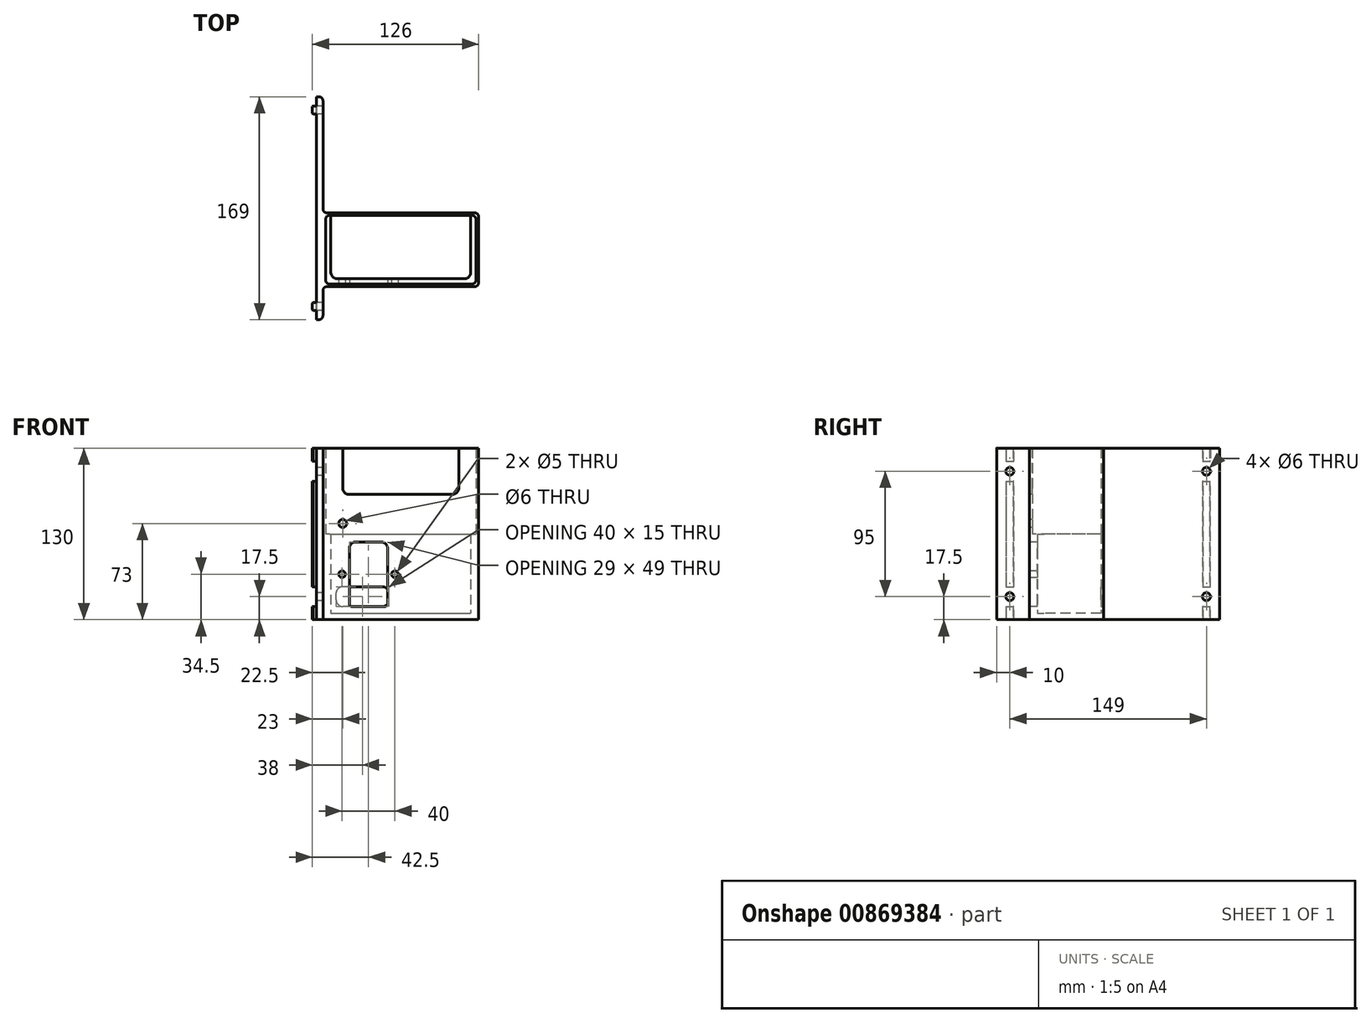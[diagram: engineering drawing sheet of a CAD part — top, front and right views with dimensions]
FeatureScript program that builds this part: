
annotation { "Feature Type Name" : "Feature", "Feature Type Description" : "" }
export const myFeature = defineFeature(function(context is Context, id is Id, definition is map)
    precondition{}
    {
        {
            var Q0;
            Q0=qCreatedBy(makeId("Top.planeOp"),FACE);
            var sketch = newSketch(context, id + "F0", { "sketchPlane" : qUnion([Q0])});
            skLineSegment(sketch, "E0.bottom", {"start": v(-57, 25) * mm, "end": v(57, 25) * mm});
            skLineSegment(sketch, "E0.top", {"start": v(-57, -27) * mm, "end": v(57, -27) * mm});
            skLineSegment(sketch, "E0.left", {"start": v(-57, 25) * mm, "end": v(-57, -27) * mm});
            skLineSegment(sketch, "E0.right", {"start": v(57, 25) * mm, "end": v(57, -27) * mm});
            skLineSegment(sketch, "E1.0", {"start": v(-59, 27) * mm, "end": v(59, 27) * mm});
            skLineSegment(sketch, "E1.1", {"start": v(-59, 27) * mm, "end": v(-59, -29) * mm});
            skLineSegment(sketch, "E1.2", {"start": v(-59, -29) * mm, "end": v(59, -29) * mm});
            skLineSegment(sketch, "E1.3", {"start": v(59, 27) * mm, "end": v(59, -29) * mm});
            skLineSegment(sketch, "E2.bottom", {"start": v(-57, 25) * mm, "end": v(-53, 25) * mm});
            skLineSegment(sketch, "E2.top", {"start": v(-57, -27) * mm, "end": v(-53, -27) * mm});
            skLineSegment(sketch, "E2.right", {"start": v(-53, 25) * mm, "end": v(-53, -23) * mm});
            skLineSegment(sketch, "E3.MirrorCS", {"start": v(53, 25) * mm, "end": v(53, -23) * mm});
            skLineSegment(sketch, "E4", {"start": v(-59, -54) * mm, "end": v(-59, 115) * mm});
            skLineSegment(sketch, "E5", {"start": v(-59, 115) * mm, "end": v(-64, 115) * mm});
            skLineSegment(sketch, "E6", {"start": v(-64, 115) * mm, "end": v(-64, -54) * mm});
            skLineSegment(sketch, "E7", {"start": v(-64, -54) * mm, "end": v(-59, -54) * mm});
            skLineSegment(sketch, "E8.bottom", {"start": v(-64, -47) * mm, "end": v(-67, -47) * mm});
            skLineSegment(sketch, "E8.top", {"start": v(-64, -41) * mm, "end": v(-67, -41) * mm});
            skLineSegment(sketch, "E8.left", {"start": v(-64, -47) * mm, "end": v(-64, -41) * mm});
            skLineSegment(sketch, "E8.right", {"start": v(-67, -47) * mm, "end": v(-67, -41) * mm});
            skLineSegment(sketch, "E9.bottom", {"start": v(-64, 108) * mm, "end": v(-67, 108) * mm});
            skLineSegment(sketch, "E9.top", {"start": v(-64, 102) * mm, "end": v(-67, 102) * mm});
            skLineSegment(sketch, "E9.left", {"start": v(-64, 108) * mm, "end": v(-64, 102) * mm});
            skLineSegment(sketch, "E9.right", {"start": v(-67, 108) * mm, "end": v(-67, 102) * mm});
            skLineSegment(sketch, "E10", {"start": v(-53, -23) * mm, "end": v(53, -23) * mm});
            skPoint(sketch, "E11.orphan", {"position": v(53, -27) * mm});
            skSolve(sketch);
        }
        {
            var Q0;
            {var subQ2=sQuery(id+"F0.wireOp",EDGE,"E1.1");Q0=makeQuery(id+"F0.imprint","IMPRINT",FACE,{"disambiguationData":[TD([[makeQuery(id+"F0.imprint","IMPRINT",EDGE,{"derivedFrom":subQ2}),-1.0]])]});}
            var Q1;
            {var subQ0=sQuery(id+"F0.wireOp",EDGE,"E8.bottom");Q1=makeQuery(id+"F0.imprint","IMPRINT",FACE,{"disambiguationData":[TD([[makeQuery(id+"F0.imprint","IMPRINT",EDGE,{"derivedFrom":subQ0}),-1.0]])]});}
            var Q2;
            {var subQ2=sQuery(id+"F0.wireOp",EDGE,"E9.bottom");Q2=makeQuery(id+"F0.imprint","IMPRINT",FACE,{"disambiguationData":[TD([[makeQuery(id+"F0.imprint","IMPRINT",EDGE,{"derivedFrom":subQ2}),1.0]])]});}
            var Q3;
            {var subQ1=sQuery(id+"F0.wireOp",EDGE,"E0.left");Q3=makeQuery(id+"F0.imprint","IMPRINT",FACE,{"disambiguationData":[TD([[makeQuery(id+"F0.imprint","IMPRINT",EDGE,{"derivedFrom":subQ1}),-1.0]])]});}
            extrude(context, id + "F1", {"entities" : qUnion([Q0, Q1, Q2, Q3]), "depth" : 130 * mm, "offsetDistance" : 25 * mm});
        }
        {
            var Q0;
            {var subQ2=sQuery(id+"F0.wireOp",EDGE,"E0.left");Q0=makeQuery(id+"F0.imprint","IMPRINT",FACE,{"disambiguationData":[TD([[makeQuery(id+"F0.imprint","IMPRINT",EDGE,{"derivedFrom":subQ2}),1.0]])]});}
            var Q1;
            {var subQ2=sQuery(id+"F0.wireOp",EDGE,"E0.left");Q1=makeQuery(id+"F0.imprint","IMPRINT",FACE,{"disambiguationData":[TD([[makeQuery(id+"F0.imprint","IMPRINT",EDGE,{"derivedFrom":subQ2}),1.0]])]});}
            extrude(context, id + "F2", {"entities" : qUnion([Q0, Q1]), "operationType" : NewBodyOperationType.ADD, "depth" : 65 * mm, "offsetDistance" : 25 * mm});
        }
        {
            var Q0;
            {var subQ0=sQuery(id+"F0.wireOp",EDGE,"E2.right");Q0=makeQuery(id+"F0.imprint","IMPRINT",FACE,{"disambiguationData":[TD([[makeQuery(id+"F0.imprint","IMPRINT",EDGE,{"derivedFrom":subQ0}),1.0]])]});}
            extrude(context, id + "F3", {"entities" : qUnion([Q0]), "operationType" : NewBodyOperationType.ADD, "depth" : 5 * mm, "offsetDistance" : 25 * mm});
        }
        {
            var Q0;
            Q0=makeQuery(id+"F1.opExtrude","SWEPT_FACE",FACE,{"disambiguationData":[OSD([sQuery(id+"F0.wireOp",EDGE,"E1.2")])]});
            var sketch = newSketch(context, id + "F4", { "sketchPlane" : qUnion([Q0])});
            skLineSegment(sketch, "E12.bottom", {"start": v(-34, 59) * mm, "end": v(-15, 59) * mm});
            skLineSegment(sketch, "E12.top", {"start": v(-37, 10) * mm, "end": v(-12, 10) * mm});
            skLineSegment(sketch, "E12.left", {"start": v(-39, 54) * mm, "end": v(-39, 12) * mm});
            skLineSegment(sketch, "E12.right", {"start": v(-10, 54) * mm, "end": v(-10, 12) * mm});
            skCircle(sketch, "E13", {"center": v(-44.5, 34.5) * mm, "radius": 2.5 * mm});
            skPoint(sketch, "E13.centerSnap0", {"position": v(-39, 34.5) * mm});
            skCircle(sketch, "E14", {"center": v(-4.5, 34.5) * mm, "radius": 2.5 * mm});
            skPoint(sketch, "E14.centerSnap0", {"position": v(-10, 34.5) * mm});
            skPoint(sketch, "E15.visualSharp", {"position": v(-10, 59) * mm});
            skArc(sketch, "E15.filletArc", {"start": v(-10, 54) * mm, "mid": v(-11.46, 57.54) * mm, "end": v(-15, 59) * mm});
            skPoint(sketch, "E16.visualSharp", {"position": v(-39, 59) * mm});
            skArc(sketch, "E16.filletArc", {"start": v(-34, 59) * mm, "mid": v(-37.54, 57.54) * mm, "end": v(-39, 54) * mm});
            skPoint(sketch, "E17.visualSharp", {"position": v(-39, 10) * mm});
            skArc(sketch, "E17.filletArc", {"start": v(-39, 12) * mm, "mid": v(-38.41, 10.59) * mm, "end": v(-37, 10) * mm});
            skPoint(sketch, "E18.visualSharp", {"position": v(-10, 10) * mm});
            skArc(sketch, "E18.filletArc", {"start": v(-12, 10) * mm, "mid": v(-10.59, 10.59) * mm, "end": v(-10, 12) * mm});
            skLineSegment(sketch, "E19.bottom", {"start": v(-44, 130) * mm, "end": v(44, 130) * mm});
            skLineSegment(sketch, "E19.top", {"start": v(-44, 95) * mm, "end": v(44, 95) * mm});
            skLineSegment(sketch, "E19.left", {"start": v(-44, 130) * mm, "end": v(-44, 95) * mm});
            skLineSegment(sketch, "E19.right", {"start": v(44, 130) * mm, "end": v(44, 95) * mm});
            skCircle(sketch, "E20", {"center": v(-44, 73) * mm, "radius": 3 * mm});
            skSolve(sketch);
        }
        {
            var Q0;
            Q0=makeQuery(id+"F4.imprint","IMPRINT",FACE,{"disambiguationData":[TD([[makeQuery(id+"F4.imprint","IMPRINT",EDGE,{"derivedFrom":sQuery(id+"F4.wireOp",EDGE,"E12.bottom")}),-1.0]])]});
            var Q1;
            Q1=makeQuery(id+"F4.imprint","IMPRINT",FACE,{"disambiguationData":[TD([[makeQuery(id+"F4.imprint","IMPRINT",EDGE,{"derivedFrom":sQuery(id+"F4.wireOp",EDGE,"E13")}),1.0]])]});
            var Q2;
            Q2=makeQuery(id+"F4.imprint","IMPRINT",FACE,{"disambiguationData":[TD([[makeQuery(id+"F4.imprint","IMPRINT",EDGE,{"derivedFrom":sQuery(id+"F4.wireOp",EDGE,"E14")}),1.0]])]});
            var Q3;
            Q3=makeQuery(id+"F4.imprint","IMPRINT",FACE,{"disambiguationData":[TD([[makeQuery(id+"F4.imprint","IMPRINT",EDGE,{"derivedFrom":sQuery(id+"F4.wireOp",EDGE,"E19.bottom")}),-1.0]])]});
            var Q4;
            Q4=makeQuery(id+"F4.imprint","IMPRINT",FACE,{"disambiguationData":[TD([[makeQuery(id+"F4.imprint","IMPRINT",EDGE,{"derivedFrom":sQuery(id+"F4.wireOp",EDGE,"E20")}),1.0]])]});
            extrude(context, id + "F5", {"entities" : qUnion([Q0, Q1, Q2, Q3, Q4]), "operationType" : NewBodyOperationType.REMOVE, "oppositeDirection" : true, "depth" : 10 * mm, "offsetDistance" : 25 * mm});
        }
        {
            var Q0;
            Q0=makeQuery(id+"F1.opExtrude","SWEPT_FACE",FACE,{"disambiguationData":[OSD([sQuery(id+"F0.wireOp",EDGE,"E1.0")])]});
            var sketch = newSketch(context, id + "F6", { "sketchPlane" : qUnion([Q0])});
            skLineSegment(sketch, "E21.bottom", {"start": v(9, 10) * mm, "end": v(49, 10) * mm});
            skLineSegment(sketch, "E21.top", {"start": v(9, 25) * mm, "end": v(49, 25) * mm});
            skLineSegment(sketch, "E21.left", {"start": v(9, 10) * mm, "end": v(9, 25) * mm});
            skLineSegment(sketch, "E21.right", {"start": v(49, 10) * mm, "end": v(49, 25) * mm});
            skSolve(sketch);
        }
        {
            var Q0;
            Q0=makeQuery(id+"F6.imprint","IMPRINT",FACE,{"disambiguationData":[TD([[makeQuery(id+"F6.imprint","IMPRINT",EDGE,{"derivedFrom":sQuery(id+"F6.wireOp",EDGE,"E21.bottom")}),1.0]])]});
            extrude(context, id + "F7", {"entities" : qUnion([Q0]), "operationType" : NewBodyOperationType.REMOVE, "oppositeDirection" : true, "depth" : 5 * mm, "offsetDistance" : 25 * mm});
        }
        {
            var Q0;
            Q0=makeQuery(id+"F1.opExtrude","SWEPT_FACE",FACE,{"disambiguationData":[OSD([sQuery(id+"F0.wireOp",EDGE,"E9.bottom")])]});
            var sketch = newSketch(context, id + "F8", { "sketchPlane" : qUnion([Q0])});
            skLineSegment(sketch, "E22.bottom", {"start": v(64, 120) * mm, "end": v(74, 120) * mm});
            skLineSegment(sketch, "E22.top", {"start": v(64, 105) * mm, "end": v(74, 105) * mm});
            skLineSegment(sketch, "E22.left", {"start": v(64, 120) * mm, "end": v(64, 105) * mm});
            skLineSegment(sketch, "E22.right", {"start": v(74, 120) * mm, "end": v(74, 105) * mm});
            skLineSegment(sketch, "E23.bottom", {"start": v(64, 10) * mm, "end": v(74, 10) * mm});
            skLineSegment(sketch, "E23.top", {"start": v(64, 25) * mm, "end": v(74, 25) * mm});
            skLineSegment(sketch, "E23.left", {"start": v(64, 10) * mm, "end": v(64, 25) * mm});
            skLineSegment(sketch, "E23.right", {"start": v(74, 10) * mm, "end": v(74, 25) * mm});
            skSolve(sketch);
        }
        {
            var Q0;
            {var subQ0=sQuery(id+"F8.wireOp",EDGE,"E23.left");Q0=makeQuery(id+"F8.imprint","IMPRINT",FACE,{"disambiguationData":[TD([[makeQuery(id+"F8.imprint","IMPRINT",EDGE,{"derivedFrom":subQ0}),1.0]])]});}
            var Q1;
            {var subQ0=sQuery(id+"F8.wireOp",EDGE,"E22.left");Q1=makeQuery(id+"F8.imprint","IMPRINT",FACE,{"disambiguationData":[TD([[makeQuery(id+"F8.imprint","IMPRINT",EDGE,{"derivedFrom":subQ0}),1.0]])]});}
            extrude(context, id + "F9", {"entities" : qUnion([Q0, Q1]), "operationType" : NewBodyOperationType.REMOVE, "oppositeDirection" : true, "depth" : 200 * mm, "offsetDistance" : 25 * mm});
        }
        {
            var Q0;
            Q0=makeQuery(id+"F1.opExtrude","SWEPT_EDGE",EDGE,{"disambiguationData":[OSD([sQuery(id+"F0.wireOp",EDGE,"E1.1"),sQuery(id+"F0.wireOp",EDGE,"E1.2"),sQuery(id+"F0.wireOp",EDGE,"E4")])]});
            var Q1;
            Q1=makeQuery(id+"F1.opExtrude","SWEPT_EDGE",EDGE,{"disambiguationData":[OSD([sQuery(id+"F0.wireOp",EDGE,"E1.0"),sQuery(id+"F0.wireOp",EDGE,"E1.1"),sQuery(id+"F0.wireOp",EDGE,"E4")])]});
            var Q2;
            Q2=makeQuery(id+"F1.opExtrude","SWEPT_EDGE",EDGE,{"disambiguationData":[OSD([sQuery(id+"F0.wireOp",EDGE,"E1.0"),sQuery(id+"F0.wireOp",EDGE,"E1.3")])]});
            var Q3;
            Q3=makeQuery(id+"F1.opExtrude","SWEPT_EDGE",EDGE,{"disambiguationData":[OSD([sQuery(id+"F0.wireOp",EDGE,"E1.2"),sQuery(id+"F0.wireOp",EDGE,"E1.3")])]});
            var Q4;
            Q4=makeQuery(id+"F1.opExtrude","SWEPT_EDGE",EDGE,{"disambiguationData":[OSD([sQuery(id+"F0.wireOp",EDGE,"E0.top"),sQuery(id+"F0.wireOp",EDGE,"E0.right")])]});
            var Q5;
            Q5=makeQuery(id+"F1.opExtrude","SWEPT_EDGE",EDGE,{"disambiguationData":[OSD([sQuery(id+"F0.wireOp",EDGE,"E0.bottom"),sQuery(id+"F0.wireOp",EDGE,"E0.right")])]});
            var Q6;
            Q6=makeQuery(id+"F1.opExtrude","SWEPT_EDGE",EDGE,{"disambiguationData":[OSD([sQuery(id+"F0.wireOp",EDGE,"E0.top"),sQuery(id+"F0.wireOp",EDGE,"E0.left")])]});
            var Q7;
            Q7=makeQuery(id+"F1.opExtrude","SWEPT_EDGE",EDGE,{"disambiguationData":[OSD([sQuery(id+"F0.wireOp",EDGE,"E0.bottom"),sQuery(id+"F0.wireOp",EDGE,"E0.left")])]});
            var Q8;
            Q8=makeQuery(id+"F1.opExtrude","SWEPT_EDGE",EDGE,{"disambiguationData":[OSD([sQuery(id+"F0.wireOp",EDGE,"E4"),sQuery(id+"F0.wireOp",EDGE,"E7")])]});
            var Q9;
            Q9=makeQuery(id+"F1.opExtrude","SWEPT_EDGE",EDGE,{"disambiguationData":[OSD([sQuery(id+"F0.wireOp",EDGE,"E4"),sQuery(id+"F0.wireOp",EDGE,"E5")])]});
            fillet(context, id + "F10", {"entities" : qUnion([Q0, Q1, Q2, Q3, Q4, Q5, Q6, Q7, Q8, Q9]), "radius" : 3 * mm, "tangentPropagation" : true, "allowEdgeOverflow" : false});
        }
        {
            var Q0;
            Q0=makeQuery(id+"F7.boolean.opBoolean","COPY",EDGE,{"derivedFrom":makeQuery(id+"F7.opExtrude","SWEPT_EDGE",EDGE,{"disambiguationData":[OSD([sQuery(id+"F6.wireOp",EDGE,"E21.top"),sQuery(id+"F6.wireOp",EDGE,"E21.left")])]})});
            var Q1;
            Q1=makeQuery(id+"F7.boolean.opBoolean","COPY",EDGE,{"derivedFrom":makeQuery(id+"F7.opExtrude","SWEPT_EDGE",EDGE,{"disambiguationData":[OSD([sQuery(id+"F6.wireOp",EDGE,"E21.bottom"),sQuery(id+"F6.wireOp",EDGE,"E21.left")])]})});
            var Q2;
            Q2=makeQuery(id+"F7.boolean.opBoolean","COPY",EDGE,{"derivedFrom":makeQuery(id+"F7.opExtrude","SWEPT_EDGE",EDGE,{"disambiguationData":[OSD([sQuery(id+"F6.wireOp",EDGE,"E21.bottom"),sQuery(id+"F6.wireOp",EDGE,"E21.right")])]})});
            var Q3;
            Q3=makeQuery(id+"F7.boolean.opBoolean","COPY",EDGE,{"derivedFrom":makeQuery(id+"F7.opExtrude","SWEPT_EDGE",EDGE,{"disambiguationData":[OSD([sQuery(id+"F6.wireOp",EDGE,"E21.top"),sQuery(id+"F6.wireOp",EDGE,"E21.right")])]})});
            var Q4;
            Q4=makeQuery(id+"F5.boolean.opBoolean","COPY",EDGE,{"derivedFrom":makeQuery(id+"F5.opExtrude","SWEPT_EDGE",EDGE,{"disambiguationData":[OSD([sQuery(id+"F4.wireOp",EDGE,"E19.top"),sQuery(id+"F4.wireOp",EDGE,"E19.left")])]})});
            var Q5;
            Q5=makeQuery(id+"F5.boolean.opBoolean","COPY",EDGE,{"derivedFrom":makeQuery(id+"F5.opExtrude","SWEPT_EDGE",EDGE,{"disambiguationData":[OSD([sQuery(id+"F4.wireOp",EDGE,"E19.top"),sQuery(id+"F4.wireOp",EDGE,"E19.right")])]})});
            var Q6;
            Q6=makeQuery(id+"F5.boolean.opBoolean","COPY",EDGE,{"derivedFrom":makeQuery(id+"F5.opExtrude","SWEPT_EDGE",EDGE,{"disambiguationData":[OSD([sQuery(id+"F0.wireOp",EDGE,"E1.2"),sQuery(id+"F4.wireOp",EDGE,"E19.bottom"),sQuery(id+"F4.wireOp",EDGE,"E19.right")])]})});
            var Q7;
            Q7=makeQuery(id+"F5.boolean.opBoolean","COPY",EDGE,{"derivedFrom":makeQuery(id+"F5.opExtrude","SWEPT_EDGE",EDGE,{"disambiguationData":[OSD([sQuery(id+"F0.wireOp",EDGE,"E1.2"),sQuery(id+"F4.wireOp",EDGE,"E19.bottom"),sQuery(id+"F4.wireOp",EDGE,"E19.left")])]})});
            fillet(context, id + "F11", {"entities" : qUnion([Q0, Q1, Q2, Q3, Q4, Q5, Q6, Q7]), "radius" : 5 * mm, "tangentPropagation" : true, "allowEdgeOverflow" : false});
        }
        {
            var Q0;
            {var subQ0=sQuery(id+"F0.wireOp",EDGE,"E6");Q0=makeQuery(id+"F9.boolean.opBoolean","MERGE",FACE,{"derivedFrom":[makeQuery(id+"F1.opExtrude","SWEPT_FACE",FACE,{"disambiguationData":[OSD([subQ0]),TDD([makeQuery(id+"F0.imprint","IMPRINT",EDGE,{"disambiguationData":[TD([[makeQuery(id+"F0.imprint","INTERSECT",VERTEX,{"derivedFrom":[subQ0,sQuery(id+"F0.wireOp",EDGE,"E9.top")]}),-1.0]])],"derivedFrom":subQ0})])]}),makeQuery(id+"F1.opExtrude","SWEPT_FACE",FACE,{"disambiguationData":[OSD([subQ0]),TDD([makeQuery(id+"F0.imprint","IMPRINT",EDGE,{"disambiguationData":[TD([[makeQuery(id+"F0.imprint","INTERSECT",VERTEX,{"derivedFrom":[subQ0,sQuery(id+"F0.wireOp",EDGE,"E8.bottom")]}),-1.0]])],"derivedFrom":subQ0})])]}),makeQuery(id+"F1.opExtrude","SWEPT_FACE",FACE,{"disambiguationData":[OSD([subQ0]),TDD([makeQuery(id+"F0.imprint","IMPRINT",EDGE,{"disambiguationData":[TD([[makeQuery(id+"F0.imprint","INTERSECT",VERTEX,{"derivedFrom":[sQuery(id+"F0.wireOp",EDGE,"E5"),subQ0]}),-1.0]])],"derivedFrom":subQ0})])]})],"fromTools":[makeQuery(id+"F9.opExtrude","SWEPT_FACE",FACE,{"disambiguationData":[OSD([sQuery(id+"F8.wireOp",EDGE,"E22.left")])]}),makeQuery(id+"F9.opExtrude","SWEPT_FACE",FACE,{"disambiguationData":[OSD([sQuery(id+"F8.wireOp",EDGE,"E23.left")])]})]});}
            var sketch = newSketch(context, id + "F12", { "sketchPlane" : qUnion([Q0])});
            skCircle(sketch, "E24", {"center": v(-105, 112.5) * mm, "radius": 3 * mm});
            skCircle(sketch, "E25", {"center": v(-105, 17.5) * mm, "radius": 3 * mm});
            skCircle(sketch, "E26", {"center": v(44, 17.5) * mm, "radius": 3 * mm});
            skPoint(sketch, "E26.centerSnap0", {"position": v(44, 25) * mm});
            skCircle(sketch, "E27", {"center": v(44, 112.5) * mm, "radius": 3 * mm});
            skSolve(sketch);
        }
        {
            var Q0;
            Q0=makeQuery(id+"F12.imprint","IMPRINT",FACE,{"disambiguationData":[TD([[makeQuery(id+"F12.imprint","IMPRINT",EDGE,{"derivedFrom":sQuery(id+"F12.wireOp",EDGE,"E24")}),1.0]])]});
            var Q1;
            Q1=makeQuery(id+"F12.imprint","IMPRINT",FACE,{"disambiguationData":[TD([[makeQuery(id+"F12.imprint","IMPRINT",EDGE,{"derivedFrom":sQuery(id+"F12.wireOp",EDGE,"E27")}),1.0]])]});
            var Q2;
            Q2=makeQuery(id+"F12.imprint","IMPRINT",FACE,{"disambiguationData":[TD([[makeQuery(id+"F12.imprint","IMPRINT",EDGE,{"derivedFrom":sQuery(id+"F12.wireOp",EDGE,"E26")}),1.0]])]});
            var Q3;
            Q3=makeQuery(id+"F12.imprint","IMPRINT",FACE,{"disambiguationData":[TD([[makeQuery(id+"F12.imprint","IMPRINT",EDGE,{"derivedFrom":sQuery(id+"F12.wireOp",EDGE,"E25")}),1.0]])]});
            extrude(context, id + "F13", {"entities" : qUnion([Q0, Q1, Q2, Q3]), "operationType" : NewBodyOperationType.REMOVE, "oppositeDirection" : true, "depth" : 25 * mm, "offsetDistance" : 25 * mm});
        }
        {
            var Q0;
            {var subQ0=sQuery(id+"F0.wireOp",EDGE,"E9.right");var subQ1=sQuery(id+"F0.wireOp",EDGE,"E9.bottom");Q0=makeQuery(id+"F9.boolean.opBoolean","SPLIT",EDGE,{"disambiguationData":[TD([makeQuery(id+"F9.opExtrude","SWEPT_FACE",FACE,{"disambiguationData":[OSD([sQuery(id+"F8.wireOp",EDGE,"E22.bottom")])]})])],"derivedFrom":makeQuery(id+"F1.opExtrude","SWEPT_EDGE",EDGE,{"disambiguationData":[OSD([subQ1,subQ0])]})});}
            var Q1;
            {var subQ0=sQuery(id+"F0.wireOp",EDGE,"E9.bottom");var subQ1=sQuery(id+"F0.wireOp",EDGE,"E9.right");Q1=makeQuery(id+"F9.boolean.opBoolean","SPLIT",EDGE,{"disambiguationData":[TD([makeQuery(id+"F9.opExtrude","SWEPT_FACE",FACE,{"disambiguationData":[OSD([sQuery(id+"F8.wireOp",EDGE,"E22.top")])]})])],"derivedFrom":makeQuery(id+"F1.opExtrude","SWEPT_EDGE",EDGE,{"disambiguationData":[OSD([subQ0,subQ1])]})});}
            var Q2;
            {var subQ0=sQuery(id+"F0.wireOp",EDGE,"E8.right");var subQ1=sQuery(id+"F0.wireOp",EDGE,"E8.top");Q2=makeQuery(id+"F9.boolean.opBoolean","SPLIT",EDGE,{"disambiguationData":[TD([makeQuery(id+"F9.opExtrude","SWEPT_FACE",FACE,{"disambiguationData":[OSD([sQuery(id+"F8.wireOp",EDGE,"E22.bottom")])]})])],"derivedFrom":makeQuery(id+"F1.opExtrude","SWEPT_EDGE",EDGE,{"disambiguationData":[OSD([subQ1,subQ0])]})});}
            var Q3;
            {var subQ0=sQuery(id+"F0.wireOp",EDGE,"E8.top");var subQ1=sQuery(id+"F0.wireOp",EDGE,"E8.right");Q3=makeQuery(id+"F9.boolean.opBoolean","SPLIT",EDGE,{"disambiguationData":[TD([makeQuery(id+"F9.opExtrude","SWEPT_FACE",FACE,{"disambiguationData":[OSD([sQuery(id+"F8.wireOp",EDGE,"E22.top")])]})])],"derivedFrom":makeQuery(id+"F1.opExtrude","SWEPT_EDGE",EDGE,{"disambiguationData":[OSD([subQ0,subQ1])]})});}
            var Q4;
            {var subQ0=sQuery(id+"F0.wireOp",EDGE,"E8.right");var subQ8=sQuery(id+"F0.wireOp",EDGE,"E8.top");Q4=makeQuery(id+"F9.boolean.opBoolean","SPLIT",EDGE,{"disambiguationData":[TD([makeQuery(id+"F9.opExtrude","SWEPT_FACE",FACE,{"disambiguationData":[OSD([sQuery(id+"F8.wireOp",EDGE,"E23.bottom")])]})])],"derivedFrom":makeQuery(id+"F1.opExtrude","SWEPT_EDGE",EDGE,{"disambiguationData":[OSD([subQ8,subQ0])]})});}
            var Q5;
            {var subQ7=sQuery(id+"F0.wireOp",EDGE,"E9.bottom");var subQ8=sQuery(id+"F0.wireOp",EDGE,"E9.right");Q5=makeQuery(id+"F9.boolean.opBoolean","SPLIT",EDGE,{"disambiguationData":[TD([makeQuery(id+"F9.opExtrude","SWEPT_FACE",FACE,{"disambiguationData":[OSD([sQuery(id+"F8.wireOp",EDGE,"E23.bottom")])]})])],"derivedFrom":makeQuery(id+"F1.opExtrude","SWEPT_EDGE",EDGE,{"disambiguationData":[OSD([subQ7,subQ8])]})});}
            var Q6;
            {var subQ7=sQuery(id+"F0.wireOp",EDGE,"E9.top");var subQ8=sQuery(id+"F0.wireOp",EDGE,"E9.right");Q6=makeQuery(id+"F9.boolean.opBoolean","SPLIT",EDGE,{"disambiguationData":[TD([makeQuery(id+"F9.opExtrude","SWEPT_FACE",FACE,{"disambiguationData":[OSD([sQuery(id+"F8.wireOp",EDGE,"E23.bottom")])]})])],"derivedFrom":makeQuery(id+"F1.opExtrude","SWEPT_EDGE",EDGE,{"disambiguationData":[OSD([subQ7,subQ8])]})});}
            var Q7;
            {var subQ0=sQuery(id+"F0.wireOp",EDGE,"E9.top");var subQ1=sQuery(id+"F0.wireOp",EDGE,"E9.right");Q7=makeQuery(id+"F9.boolean.opBoolean","SPLIT",EDGE,{"disambiguationData":[TD([makeQuery(id+"F9.opExtrude","SWEPT_FACE",FACE,{"disambiguationData":[OSD([sQuery(id+"F8.wireOp",EDGE,"E22.top")])]})])],"derivedFrom":makeQuery(id+"F1.opExtrude","SWEPT_EDGE",EDGE,{"disambiguationData":[OSD([subQ0,subQ1])]})});}
            var Q8;
            {var subQ0=sQuery(id+"F0.wireOp",EDGE,"E9.right");var subQ1=sQuery(id+"F0.wireOp",EDGE,"E9.top");Q8=makeQuery(id+"F9.boolean.opBoolean","SPLIT",EDGE,{"disambiguationData":[TD([makeQuery(id+"F9.opExtrude","SWEPT_FACE",FACE,{"disambiguationData":[OSD([sQuery(id+"F8.wireOp",EDGE,"E22.bottom")])]})])],"derivedFrom":makeQuery(id+"F1.opExtrude","SWEPT_EDGE",EDGE,{"disambiguationData":[OSD([subQ1,subQ0])]})});}
            var Q9;
            {var subQ0=sQuery(id+"F0.wireOp",EDGE,"E8.right");var subQ1=sQuery(id+"F0.wireOp",EDGE,"E8.bottom");Q9=makeQuery(id+"F9.boolean.opBoolean","SPLIT",EDGE,{"disambiguationData":[TD([makeQuery(id+"F9.opExtrude","SWEPT_FACE",FACE,{"disambiguationData":[OSD([sQuery(id+"F8.wireOp",EDGE,"E22.bottom")])]})])],"derivedFrom":makeQuery(id+"F1.opExtrude","SWEPT_EDGE",EDGE,{"disambiguationData":[OSD([subQ1,subQ0])]})});}
            var Q10;
            {var subQ0=sQuery(id+"F0.wireOp",EDGE,"E8.bottom");var subQ1=sQuery(id+"F0.wireOp",EDGE,"E8.right");Q10=makeQuery(id+"F9.boolean.opBoolean","SPLIT",EDGE,{"disambiguationData":[TD([makeQuery(id+"F9.opExtrude","SWEPT_FACE",FACE,{"disambiguationData":[OSD([sQuery(id+"F8.wireOp",EDGE,"E22.top")])]})])],"derivedFrom":makeQuery(id+"F1.opExtrude","SWEPT_EDGE",EDGE,{"disambiguationData":[OSD([subQ0,subQ1])]})});}
            var Q11;
            {var subQ7=sQuery(id+"F0.wireOp",EDGE,"E8.bottom");var subQ8=sQuery(id+"F0.wireOp",EDGE,"E8.right");Q11=makeQuery(id+"F9.boolean.opBoolean","SPLIT",EDGE,{"disambiguationData":[TD([makeQuery(id+"F9.opExtrude","SWEPT_FACE",FACE,{"disambiguationData":[OSD([sQuery(id+"F8.wireOp",EDGE,"E23.bottom")])]})])],"derivedFrom":makeQuery(id+"F1.opExtrude","SWEPT_EDGE",EDGE,{"disambiguationData":[OSD([subQ7,subQ8])]})});}
            chamfer(context, id + "F14", {"entities" : qUnion([Q0, Q1, Q2, Q3, Q4, Q5, Q6, Q7, Q8, Q9, Q10, Q11]), "width" : .5 * mm, "tangentPropagation" : true});
        }
        {
            var Q0;
            Q0=makeQuery(id+"F2.opExtrude","SWEPT_EDGE",EDGE,{"disambiguationData":[OSD([sQuery(id+"F0.wireOp",EDGE,"E0.bottom"),sQuery(id+"F0.wireOp",EDGE,"E2.right")])]});
            var Q1;
            Q1=makeQuery(id+"F2.opExtrude","SWEPT_EDGE",EDGE,{"disambiguationData":[OSD([sQuery(id+"F0.wireOp",EDGE,"E2.right"),sQuery(id+"F0.wireOp",EDGE,"E10")])]});
            var Q2;
            Q2=makeQuery(id+"F2.opExtrude","SWEPT_EDGE",EDGE,{"disambiguationData":[OSD([sQuery(id+"F0.wireOp",EDGE,"E3.MirrorCS"),sQuery(id+"F0.wireOp",EDGE,"E10")])]});
            var Q3;
            Q3=makeQuery(id+"F2.opExtrude","SWEPT_EDGE",EDGE,{"disambiguationData":[OSD([sQuery(id+"F0.wireOp",EDGE,"E0.bottom"),sQuery(id+"F0.wireOp",EDGE,"E3.MirrorCS")])]});
            fillet(context, id + "F15", {"entities" : qUnion([Q0, Q1, Q2, Q3]), "radius" : 5 * mm, "tangentPropagation" : true, "allowEdgeOverflow" : false});
        }
    });
